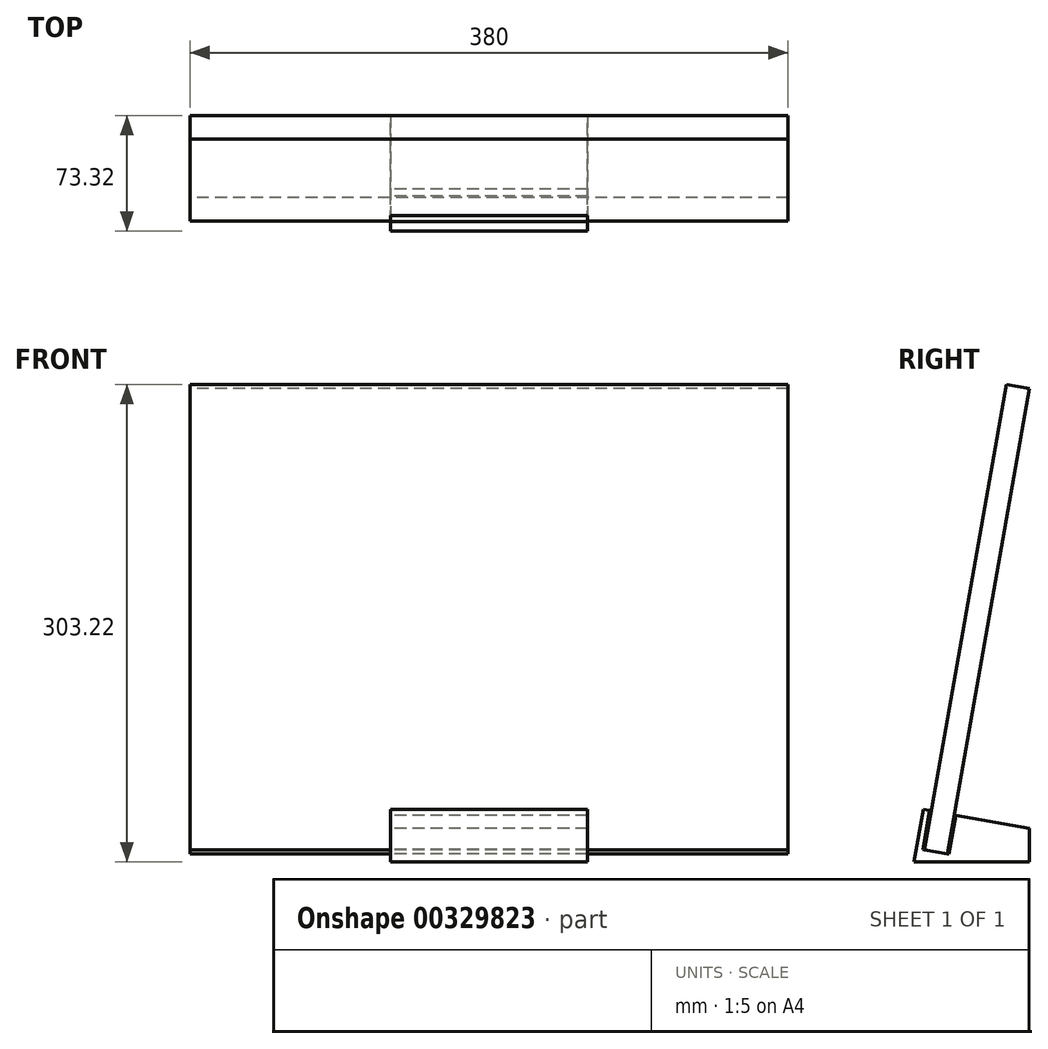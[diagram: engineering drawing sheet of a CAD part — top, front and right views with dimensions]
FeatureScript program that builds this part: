
annotation { "Feature Type Name" : "Feature", "Feature Type Description" : "" }
export const myFeature = defineFeature(function(context is Context, id is Id, definition is map)
    precondition{}
    {
        {
            var Q0;
            Q0=qCreatedBy(makeId("Right.planeOp"),FACE);
            var sketch = newSketch(context, id + "F0", { "sketchPlane" : qUnion([Q0])});
            skLineSegment(sketch, "E0", {"start": v(0, 2.6) * mm, "end": v(14.77, 0) * mm});
            skLineSegment(sketch, "E1", {"start": v(14.77, 0) * mm, "end": v(66.87, 295.44) * mm});
            skLineSegment(sketch, "E2", {"start": v(66.87, 295.44) * mm, "end": v(52.1, 298.05) * mm});
            skLineSegment(sketch, "E3", {"start": v(52.1, 298.05) * mm, "end": v(0, 2.6) * mm});
            skSolve(sketch);
        }
        {
            var Q0;
            Q0=makeQuery(id+"F0.imprint","IMPRINT",FACE,{"disambiguationData":[TD([[makeQuery(id+"F0.imprint","IMPRINT",EDGE,{"derivedFrom":sQuery(id+"F0.wireOp",EDGE,"E0")}),1.0]])]});
            extrude(context, id + "F1", {"entities" : qUnion([Q0]), "depth" : 380 * mm, "symmetric" : true});
        }
        {
            var Q0;
            Q0=qCreatedBy(makeId("Right.planeOp"),FACE);
            var sketch = newSketch(context, id + "F2", { "sketchPlane" : qUnion([Q0])});
            skLineSegment(sketch, "E4", {"start": v(3.36, 27.4) * mm, "end": v(-0.98, 2.78) * mm});
            skLineSegment(sketch, "E5", {"start": v(-0.98, 2.78) * mm, "end": v(15.76, -0.17) * mm});
            skLineSegment(sketch, "E6", {"start": v(15.76, -0.17) * mm, "end": v(20.1, 24.45) * mm});
            skLineSegment(sketch, "E7", {"start": v(20.1, 24.45) * mm, "end": v(66.87, 16.2) * mm});
            skLineSegment(sketch, "E8", {"start": v(66.87, 16.2) * mm, "end": v(66.87, -5.17) * mm});
            skLineSegment(sketch, "E9", {"start": v(66.87, -5.17) * mm, "end": v(-6.45, -5.17) * mm});
            skLineSegment(sketch, "E10", {"start": v(-6.45, -5.17) * mm, "end": v(-0.58, 28.1) * mm});
            skLineSegment(sketch, "E11", {"start": v(-0.58, 28.1) * mm, "end": v(3.36, 27.4) * mm});
            skLineSegment(sketch, "E12", {"start": v(3.36, 27.4) * mm, "end": v(20.1, 24.45) * mm, "construction": true});
            skSolve(sketch);
        }
        {
            var Q0;
            Q0 = qSketchRegion(id + "F2", true);
            extrude(context, id + "F3", {"entities" : qUnion([Q0]), "depth" : 125 * mm, "symmetric" : true});
        }
    });
